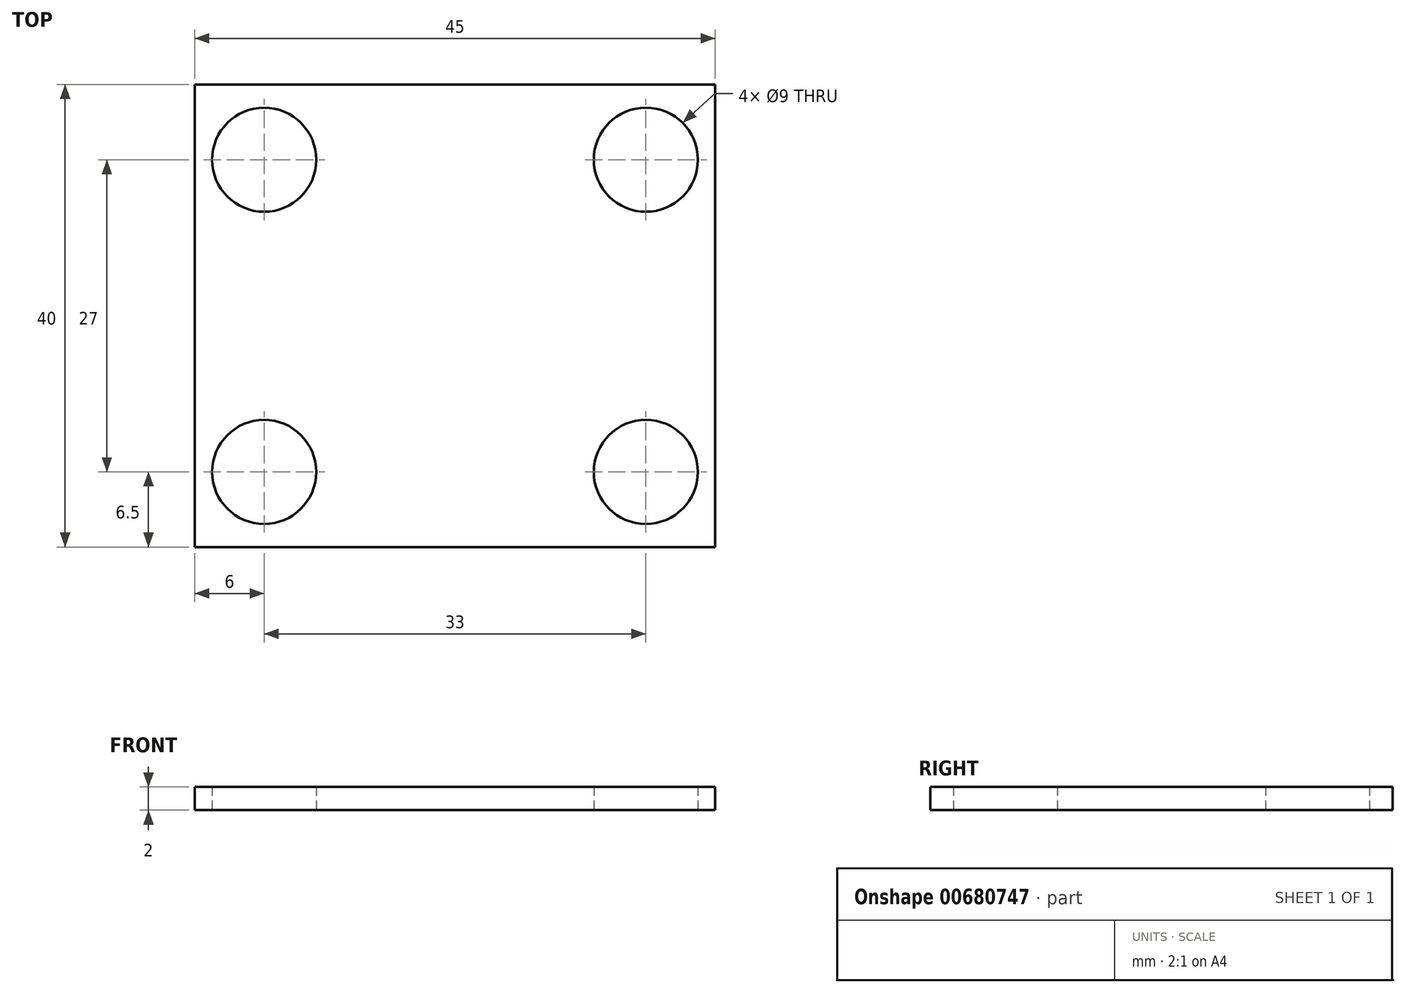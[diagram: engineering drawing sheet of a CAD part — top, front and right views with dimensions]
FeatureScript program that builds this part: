
annotation { "Feature Type Name" : "Feature", "Feature Type Description" : "" }
export const myFeature = defineFeature(function(context is Context, id is Id, definition is map)
    precondition{}
    {
        {
            var Q0;
            Q0=qCreatedBy(makeId("Top.planeOp"),FACE);
            var sketch = newSketch(context, id + "F0", { "sketchPlane" : qUnion([Q0])});
            skLineSegment(sketch, "E0.bottom", {"start": v(22.5, 20) * mm, "end": v(-22.5, 20) * mm});
            skLineSegment(sketch, "E0.top", {"start": v(22.5, -20) * mm, "end": v(-22.5, -20) * mm});
            skLineSegment(sketch, "E0.left", {"start": v(22.5, 20) * mm, "end": v(22.5, -20) * mm});
            skLineSegment(sketch, "E0.right", {"start": v(-22.5, 20) * mm, "end": v(-22.5, -20) * mm});
            skPoint(sketch, "E0.middle", {"position": v(0, 0) * mm});
            skLineSegment(sketch, "E1", {"start": v(0, -29.39) * mm, "end": v(0, 39) * mm, "construction": true});
            skLineSegment(sketch, "E2", {"start": v(-32.9, 0) * mm, "end": v(46.89, 0) * mm, "construction": true});
            skCircle(sketch, "E3", {"center": v(16.5, 13.5) * mm, "radius": 4.5 * mm});
            skCircle(sketch, "E4.MirrorC", {"center": v(-16.5, 13.5) * mm, "radius": 4.5 * mm});
            skCircle(sketch, "E5.MirrorC", {"center": v(-16.5, -13.5) * mm, "radius": 4.5 * mm});
            skCircle(sketch, "E6.MirrorC", {"center": v(16.5, -13.5) * mm, "radius": 4.5 * mm});
            skSolve(sketch);
        }
        {
            var Q0;
            Q0=makeQuery(id+"F0.imprint","IMPRINT",FACE,{"disambiguationData":[TD([[makeQuery(id+"F0.imprint","IMPRINT",EDGE,{"derivedFrom":sQuery(id+"F0.wireOp",EDGE,"E0.bottom")}),1.0]])]});
            extrude(context, id + "F1", {"entities" : qUnion([Q0]), "depth" : 2 * mm, "offsetDistance" : 25 * mm});
        }
    });
